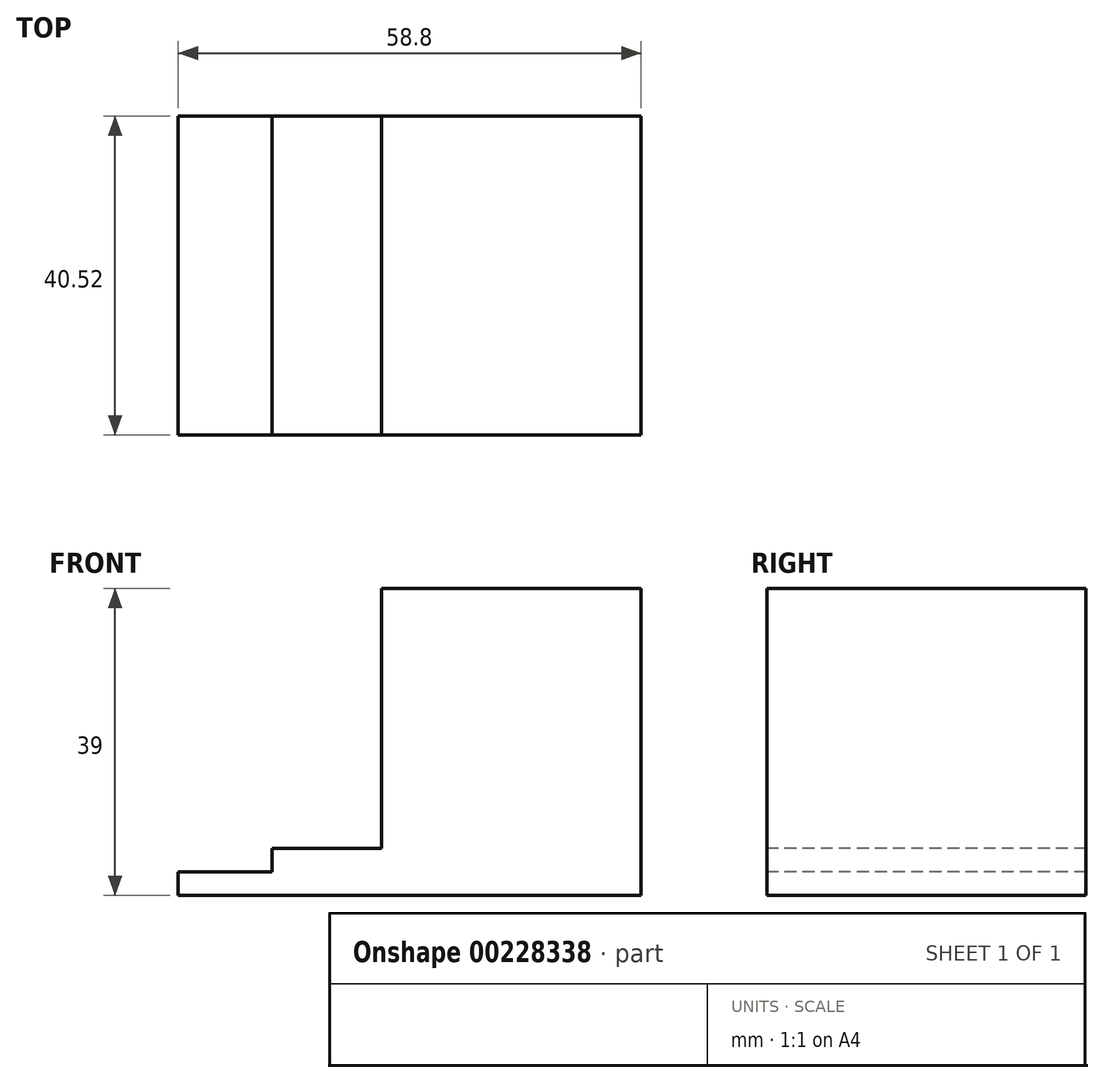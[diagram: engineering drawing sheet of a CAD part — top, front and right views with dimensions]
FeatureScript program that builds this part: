
annotation { "Feature Type Name" : "Feature", "Feature Type Description" : "" }
export const myFeature = defineFeature(function(context is Context, id is Id, definition is map)
    precondition{}
    {
        {
            var Q0;
            Q0=qCreatedBy(makeId("Top.planeOp"),FACE);
            var sketch = newSketch(context, id + "F0", { "sketchPlane" : qUnion([Q0])});
            skLineSegment(sketch, "E0.bottom", {"start": v(-29.4, 20.26) * mm, "end": v(29.4, 20.26) * mm});
            skLineSegment(sketch, "E0.top", {"start": v(-29.4, -20.26) * mm, "end": v(29.4, -20.26) * mm});
            skLineSegment(sketch, "E0.left", {"start": v(-29.4, 20.26) * mm, "end": v(-29.4, -20.26) * mm});
            skLineSegment(sketch, "E0.right", {"start": v(29.4, 20.26) * mm, "end": v(29.4, -20.26) * mm});
            skPoint(sketch, "E0.middle", {"position": v(0, 0) * mm});
            skSolve(sketch);
        }
        {
            var Q0;
            Q0 = qSketchRegion(id + "F0", true);
            extrude(context, id + "F1", {"entities" : qUnion([Q0]), "depth" : 3 * mm});
        }
        {
            var Q0;
            Q0=makeQuery(id+"F1.opExtrude","CAP_FACE",FACE,{"disambiguationData":[OSD([sQuery(id+"F0.wireOp",EDGE,"E0.bottom"),sQuery(id+"F0.wireOp",EDGE,"E0.top"),sQuery(id+"F0.wireOp",EDGE,"E0.left"),sQuery(id+"F0.wireOp",EDGE,"E0.right")])],"isStart":false});
            var sketch = newSketch(context, id + "F2", { "sketchPlane" : qUnion([Q0])});
            skLineSegment(sketch, "E1.bottom", {"start": v(29.4, 20.26) * mm, "end": v(-17.48, 20.26) * mm});
            skLineSegment(sketch, "E1.top", {"start": v(29.4, -20.26) * mm, "end": v(-17.48, -20.26) * mm});
            skLineSegment(sketch, "E1.left", {"start": v(29.4, 20.26) * mm, "end": v(29.4, -20.26) * mm});
            skLineSegment(sketch, "E1.right", {"start": v(-17.48, 20.26) * mm, "end": v(-17.48, -20.26) * mm});
            skSolve(sketch);
        }
        {
            var Q0;
            Q0 = qSketchRegion(id + "F2", true);
            extrude(context, id + "F3", {"entities" : qUnion([Q0]), "operationType" : NewBodyOperationType.ADD, "depth" : 3 * mm});
        }
        {
            var Q0;
            Q0=makeQuery(id+"F3.opExtrude","CAP_FACE",FACE,{"disambiguationData":[OSD([sQuery(id+"F2.wireOp",EDGE,"E1.bottom"),sQuery(id+"F2.wireOp",EDGE,"E1.top"),sQuery(id+"F2.wireOp",EDGE,"E1.left"),sQuery(id+"F2.wireOp",EDGE,"E1.right")])],"isStart":false});
            var sketch = newSketch(context, id + "F4", { "sketchPlane" : qUnion([Q0])});
            skLineSegment(sketch, "E2.bottom", {"start": v(29.4, 20.26) * mm, "end": v(-3.6, 20.26) * mm});
            skLineSegment(sketch, "E2.top", {"start": v(29.4, -20.26) * mm, "end": v(-3.6, -20.26) * mm});
            skLineSegment(sketch, "E2.left", {"start": v(29.4, 20.26) * mm, "end": v(29.4, -20.26) * mm});
            skLineSegment(sketch, "E2.right", {"start": v(-3.6, 20.26) * mm, "end": v(-3.6, -20.26) * mm});
            skSolve(sketch);
        }
        {
            var Q0;
            Q0 = qSketchRegion(id + "F4", true);
            extrude(context, id + "F5", {"entities" : qUnion([Q0]), "operationType" : NewBodyOperationType.ADD, "depth" : 3 * mm});
        }
        {
            var Q0;
            Q0=makeQuery(id+"F5.opExtrude","CAP_FACE",FACE,{"disambiguationData":[OSD([sQuery(id+"F4.wireOp",EDGE,"E2.bottom"),sQuery(id+"F4.wireOp",EDGE,"E2.top"),sQuery(id+"F4.wireOp",EDGE,"E2.left"),sQuery(id+"F4.wireOp",EDGE,"E2.right")])],"isStart":false});
            var sketch = newSketch(context, id + "F6", { "sketchPlane" : qUnion([Q0])});
            skSolve(sketch);
        }
        {
            var Q0;
            Q0=makeQuery(id+"F6.imprint","IMPRINT",FACE,{"disambiguationData":[TD([[makeQuery(id+"F6.imprint","IMPRINT",EDGE,{"derivedFrom":makeQuery(id+"F5.opExtrude","CAP_EDGE",EDGE,{"disambiguationData":[OSD([sQuery(id+"F4.wireOp",EDGE,"E2.bottom")])],"isStart":false})}),-1.0]])]});
            extrude(context, id + "F7", {"entities" : qUnion([Q0]), "operationType" : NewBodyOperationType.ADD, "depth" : 30 * mm});
        }
    });
